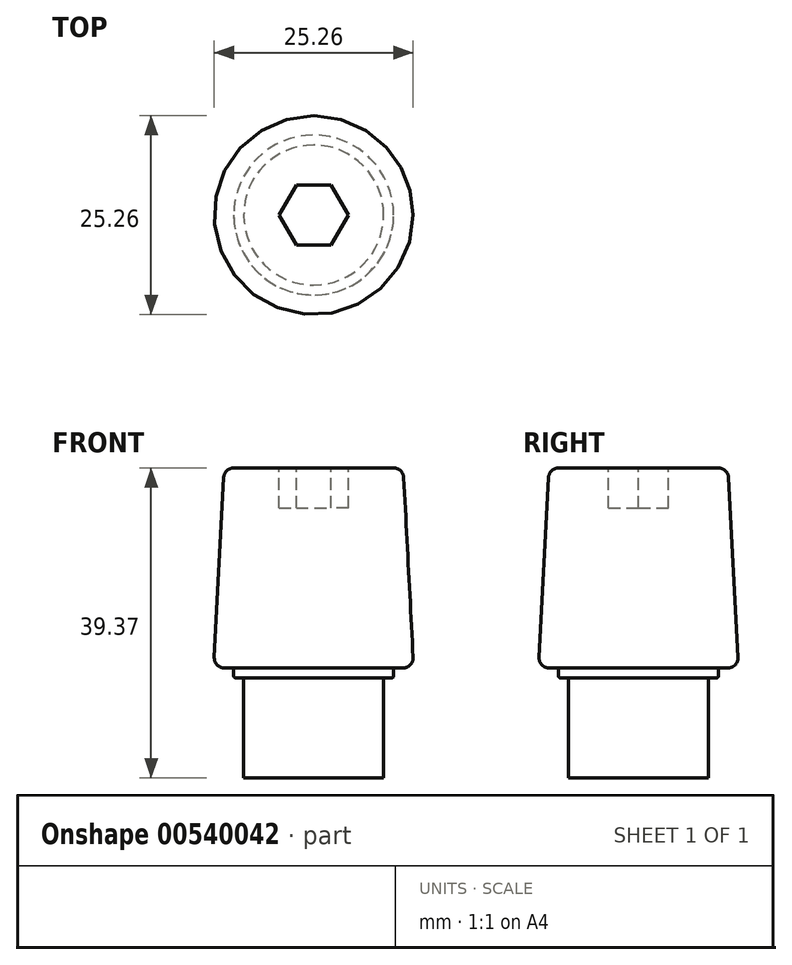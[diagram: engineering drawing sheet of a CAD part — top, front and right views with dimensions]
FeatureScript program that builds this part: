
annotation { "Feature Type Name" : "Feature", "Feature Type Description" : "" }
export const myFeature = defineFeature(function(context is Context, id is Id, definition is map)
    precondition{}
    {
        {
            var Q0;
            Q0=qCreatedBy(makeId("Top.planeOp"),FACE);
            var sketch = newSketch(context, id + "F0", { "sketchPlane" : qUnion([Q0])});
            skCircle(sketch, "E0", {"center": v(0, 0) * mm, "radius": 12.7 * mm});
            skSolve(sketch);
        }
        {
            var Q0;
            Q0 = qSketchRegion(id + "F0", true);
            var Q1;
            Q1=sQuery(id+"F0.wireOp",EDGE,"E0");
            extrude(context, id + "F1", {"entities" : qUnion([Q0]), "surfaceEntities" : qUnion([Q1]), "depth" : 25.4 * mm, "offsetDistance" : 25.4 * mm, "hasDraft" : true, "draftAngle" : 3 * degree, "draftPullDirection" : true});
        }
        {
            var Q0;
            Q0=makeQuery(id+"F1.opExtrude","CAP_FACE",FACE,{"disambiguationData":[OSD([sQuery(id+"F0.wireOp",EDGE,"E0")])],"isStart":false});
            var sketch = newSketch(context, id + "F2", { "sketchPlane" : qUnion([Q0])});
            skCircle(sketch, "E1.cCircle", {"center": v(0, 0) * mm, "radius": 3.81 * mm, "construction": true});
            skLineSegment(sketch, "E1.0", {"start": v(-2.2, 3.8) * mm, "end": v(2.2, 3.81) * mm});
            skLineSegment(sketch, "E1.1", {"start": v(2.2, 3.8) * mm, "end": v(4.4, 0) * mm});
            skLineSegment(sketch, "E1.2", {"start": v(4.4, 0) * mm, "end": v(2.2, -3.81) * mm});
            skLineSegment(sketch, "E1.3", {"start": v(2.2, -3.81) * mm, "end": v(-2.2, -3.81) * mm});
            skLineSegment(sketch, "E1.4", {"start": v(-2.2, -3.81) * mm, "end": v(-4.4, 0) * mm});
            skLineSegment(sketch, "E1.5", {"start": v(-4.4, 0) * mm, "end": v(-2.2, 3.8) * mm});
            skPoint(sketch, "E1.0.midPoint", {"position": v(0, 3.8) * mm});
            skSolve(sketch);
        }
        {
            var Q0;
            Q0 = qSketchRegion(id + "F2", true);
            extrude(context, id + "F3", {"entities" : qUnion([Q0]), "operationType" : NewBodyOperationType.REMOVE, "oppositeDirection" : true, "depth" : 5.08 * mm, "offsetDistance" : 25.4 * mm});
        }
        {
            var Q0;
            Q0=makeQuery(id+"F1.opExtrude","CAP_EDGE",EDGE,{"disambiguationData":[OSD([sQuery(id+"F0.wireOp",EDGE,"E0")])],"isStart":false});
            fillet(context, id + "F4", {"entities" : qUnion([Q0]), "radius" : 1.27 * mm, "tangentPropagation" : true, "allowEdgeOverflow" : false});
        }
        {
            var Q0;
            Q0=makeQuery(id+"F1.opExtrude","CAP_EDGE",EDGE,{"disambiguationData":[OSD([sQuery(id+"F0.wireOp",EDGE,"E0")])],"isStart":true});
            fillet(context, id + "F5", {"entities" : qUnion([Q0]), "radius" : 1.27 * mm, "tangentPropagation" : true, "allowEdgeOverflow" : false});
        }
        {
            var Q0;
            Q0=makeQuery(id+"F1.opExtrude","CAP_FACE",FACE,{"disambiguationData":[OSD([sQuery(id+"F0.wireOp",EDGE,"E0")])],"isStart":true});
            var sketch = newSketch(context, id + "F6", { "sketchPlane" : qUnion([Q0])});
            skSolve(sketch);
        }
        {
            var Q0;
            {var subQ0=sQuery(id+"F0.wireOp",EDGE,"E0");Q0=makeQuery(id+"F6.imprint","IMPRINT",FACE,{"disambiguationData":[TD([[makeQuery(id+"F6.imprint","IMPRINT",EDGE,{"derivedFrom":makeQuery(id+"F5.opFillet","BLEND_EDGE",EDGE,{"blendedFrom":[makeQuery(id+"F1.opExtrude","CAP_EDGE",EDGE,{"disambiguationData":[OSD([subQ0])],"isStart":true}),makeQuery(id+"F1.opExtrude","CAP_FACE",FACE,{"disambiguationData":[OSD([subQ0])],"isStart":true})],"blendedInto":[makeQuery(id+"F1.opExtrude","CAP_FACE",FACE,{"disambiguationData":[OSD([subQ0])],"isStart":true})]})}),1.0]])]});}
            var sketch = newSketch(context, id + "F7", { "sketchPlane" : qUnion([Q0])});
            skCircle(sketch, "E2", {"center": v(0, 0) * mm, "radius": 10.16 * mm});
            skSolve(sketch);
        }
        {
            var Q0;
            Q0 = qSketchRegion(id + "F7", true);
            extrude(context, id + "F8", {"entities" : qUnion([Q0]), "operationType" : NewBodyOperationType.ADD, "depth" : 1.27 * mm, "offsetDistance" : 25.4 * mm});
        }
        {
            var Q0;
            Q0=makeQuery(id+"F8.opExtrude","CAP_EDGE",EDGE,{"disambiguationData":[OSD([sQuery(id+"F7.wireOp",EDGE,"E2")])],"isStart":false});
            fillet(context, id + "F9", {"entities" : qUnion([Q0]), "radius" : 0.25 * mm, "tangentPropagation" : true, "allowEdgeOverflow" : false});
        }
        {
            var Q0;
            Q0=makeQuery(id+"F8.opExtrude","CAP_FACE",FACE,{"disambiguationData":[OSD([sQuery(id+"F7.wireOp",EDGE,"E2")])],"isStart":false});
            var sketch = newSketch(context, id + "F10", { "sketchPlane" : qUnion([Q0])});
            skCircle(sketch, "E3", {"center": v(0, 0) * mm, "radius": 8.9 * mm});
            skSolve(sketch);
        }
        {
            var Q0;
            Q0 = qSketchRegion(id + "F10", true);
            extrude(context, id + "F11", {"entities" : qUnion([Q0]), "operationType" : NewBodyOperationType.ADD, "depth" : 12.7 * mm, "offsetDistance" : 25.4 * mm});
        }
    });
